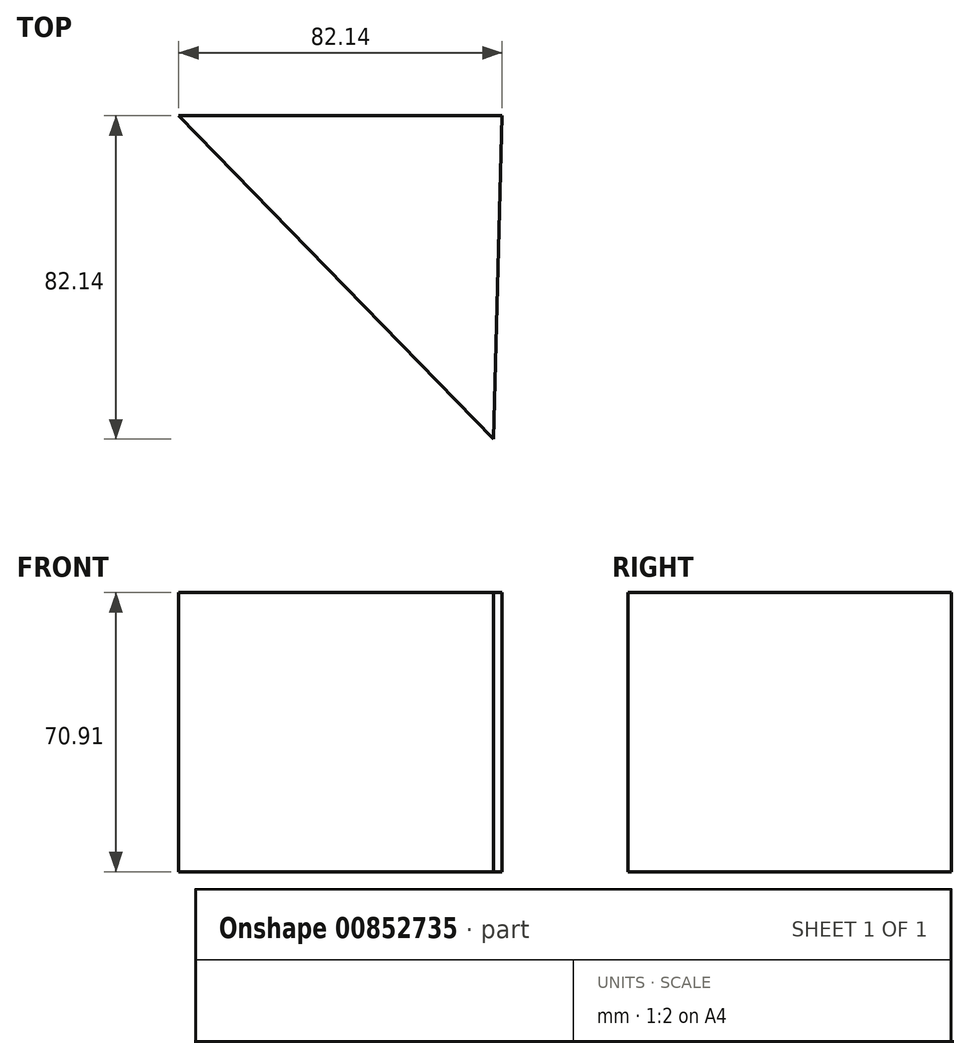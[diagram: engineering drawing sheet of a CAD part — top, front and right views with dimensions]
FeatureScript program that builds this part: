
annotation { "Feature Type Name" : "Feature", "Feature Type Description" : "" }
export const myFeature = defineFeature(function(context is Context, id is Id, definition is map)
    precondition{}
    {
        {
            var Q0;
            Q0=qCreatedBy(makeId("Top.planeOp"),FACE);
            var sketch = newSketch(context, id + "F0", { "sketchPlane" : qUnion([Q0])});
            skLineSegment(sketch, "E0", {"start": v(-31.28, 40.34) * mm, "end": v(-31.28, 40.34) * mm});
            skLineSegment(sketch, "E1", {"start": v(-31.28, 40.34) * mm, "end": v(50.86, 40.34) * mm});
            skLineSegment(sketch, "E2", {"start": v(50.86, 40.34) * mm, "end": v(48.63, -41.8) * mm});
            skLineSegment(sketch, "E3", {"start": v(48.63, -41.8) * mm, "end": v(-31.28, 40.34) * mm});
            skSolve(sketch);
        }
        {
            var Q0;
            Q0=makeQuery(id+"F0.imprint","IMPRINT",FACE,{"disambiguationData":[TD([[makeQuery(id+"F0.imprint","IMPRINT",EDGE,{"derivedFrom":sQuery(id+"F0.wireOp",EDGE,"E1")}),-1.0]])]});
            var sketch = newSketch(context, id + "F1", { "sketchPlane" : qUnion([Q0])});
            skSolve(sketch);
        }
        {
            var Q0;
            Q0=makeQuery(id+"F1.imprint","IMPRINT",FACE,{"disambiguationData":[TD([[makeQuery(id+"F1.imprint","IMPRINT",EDGE,{"derivedFrom":makeQuery(id+"F0.imprint","IMPRINT",EDGE,{"derivedFrom":sQuery(id+"F0.wireOp",EDGE,"E1")})}),-1.0]])]});
            extrude(context, id + "F2", {"entities" : qUnion([Q0]), "oppositeDirection" : true, "depth" : 70.9 * mm, "offsetDistance" : 25.4 * mm});
        }
    });
